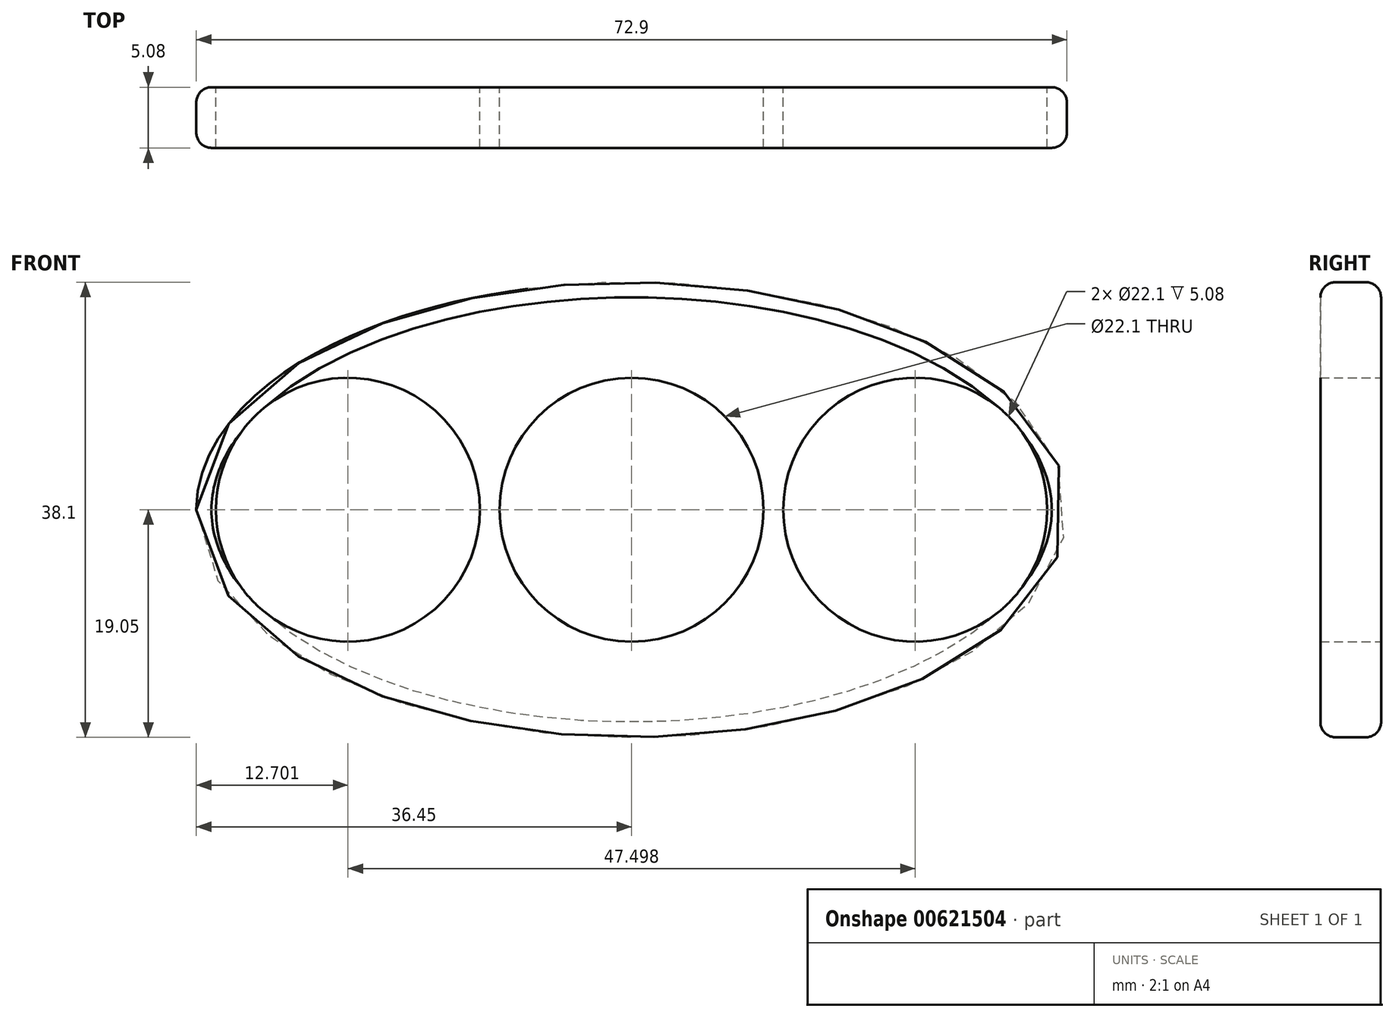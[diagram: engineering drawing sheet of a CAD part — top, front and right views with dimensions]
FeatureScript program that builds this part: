
annotation { "Feature Type Name" : "Feature", "Feature Type Description" : "" }
export const myFeature = defineFeature(function(context is Context, id is Id, definition is map)
    precondition{}
    {
        {
            var Q0;
            Q0=qCreatedBy(makeId("Front.planeOp"),FACE);
            var sketch = newSketch(context, id + "F0", { "sketchPlane" : qUnion([Q0])});
            skCircle(sketch, "E0", {"center": v(0, 0) * mm, "radius": 11.05 * mm});
            skEllipse(sketch, "E1", {"center": v(0, 0) * mm, "majorRadius": 36.45 * mm, "minorRadius": 19.05 * mm, "majorAxis": v(-1, 0)});
            skCircle(sketch, "E2", {"center": v(-23.75, 0) * mm, "radius": 11.05 * mm});
            skCircle(sketch, "E3", {"center": v(23.75, 0) * mm, "radius": 11.05 * mm});
            skPoint(sketch, "E4.start.orphan", {"position": v(-11.05, 0) * mm});
            skPoint(sketch, "E5.trimOffspring.end.orphan", {"position": v(-36.45, 0) * mm});
            skPoint(sketch, "E6.trimOffspring.end.orphan", {"position": v(36.45, 0) * mm});
            skPoint(sketch, "E7.start.orphan", {"position": v(11.05, 0) * mm});
            skSolve(sketch);
        }
        {
            var Q0;
            Q0=makeQuery(id+"F0.imprint","IMPRINT",FACE,{"disambiguationData":[TD([[makeQuery(id+"F0.imprint","IMPRINT",EDGE,{"derivedFrom":sQuery(id+"F0.wireOp",EDGE,"E0")}),-1.0]])]});
            extrude(context, id + "F1", {"entities" : qUnion([Q0]), "depth" : 5.08 * mm, "offsetDistance" : 25.4 * mm});
        }
        {
            var Q0;
            Q0=makeQuery(id+"F1.opExtrude","CAP_EDGE",EDGE,{"disambiguationData":[OSD([sQuery(id+"F0.wireOp",EDGE,"E1")])],"isStart":true});
            fillet(context, id + "F2", {"entities" : qUnion([Q0]), "radius" : 1.27 * mm, "tangentPropagation" : true, "allowEdgeOverflow" : false});
        }
        {
            var Q0;
            Q0=makeQuery(id+"F1.opExtrude","CAP_EDGE",EDGE,{"disambiguationData":[OSD([sQuery(id+"F0.wireOp",EDGE,"E1")])],"isStart":false});
            fillet(context, id + "F3", {"entities" : qUnion([Q0]), "radius" : 1.27 * mm, "tangentPropagation" : true, "allowEdgeOverflow" : false});
        }
    });
